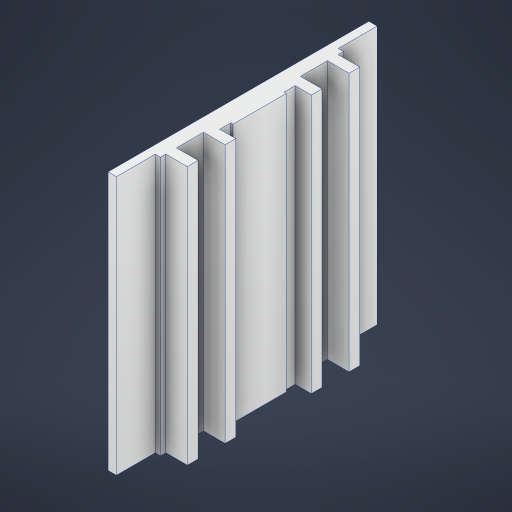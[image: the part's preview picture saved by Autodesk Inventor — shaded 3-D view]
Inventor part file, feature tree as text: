
AUTODESK INVENTOR PART (.ipt)
format: ipt  version: 2024 (Build 280153000, 153)  size: 253,440 bytes
history: native  units: mm
features: extrude x1, mirror x1, sketch x1
ambient origin geometry x8: Origin, YZ Plane, XZ Plane, XY Plane, X Axis, Y Axis, Z Axis, Center Point
bodies: Solid1 (feature_tree)
feature tree (3):
  extrude  "Extrusion1"  Depth=240.0mm TaperAngle=0.0deg
  mirror  "Mirror1"
  sketch  "Sketch1"  dims[d3=5.0mm d5=240.0mm d6=0.0mm d8=10.0mm d9=36.0mm d13=45.0mm d14=24.8mm d15=10.0mm d17=5.0mm d18=2.1mm d19=10.2mm d21=35.0mm]
